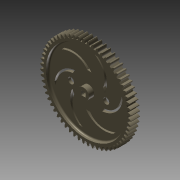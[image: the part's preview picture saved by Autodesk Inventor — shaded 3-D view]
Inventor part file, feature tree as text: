
AUTODESK INVENTOR PART (.ipt)
format: ipt  version: 2013 (Build 170138000, 138)  size: 1,093,632 bytes
history: native  units: mm (DEFAULTED — no unit token found)
features: imported_body x1, sketch x1, other x1, extrude x1
ambient origin geometry x8: Origin, YZ Plane, XZ Plane, XY Plane, X Axis, Y Axis, Z Axis, Center Point
bodies: Solid1 (feature_tree)
feature tree (4):
  imported_body  "Base1"
  sketch  "Sketch1"  dims[d1=8.001mm d5=25.4mm d6=0.0mm d7=0.0mm d8=0.0mm]
  other  "Srf1"
  extrude  "ExtrusionSrf1"  Depth=25.4mm TaperAngle=0.0deg
